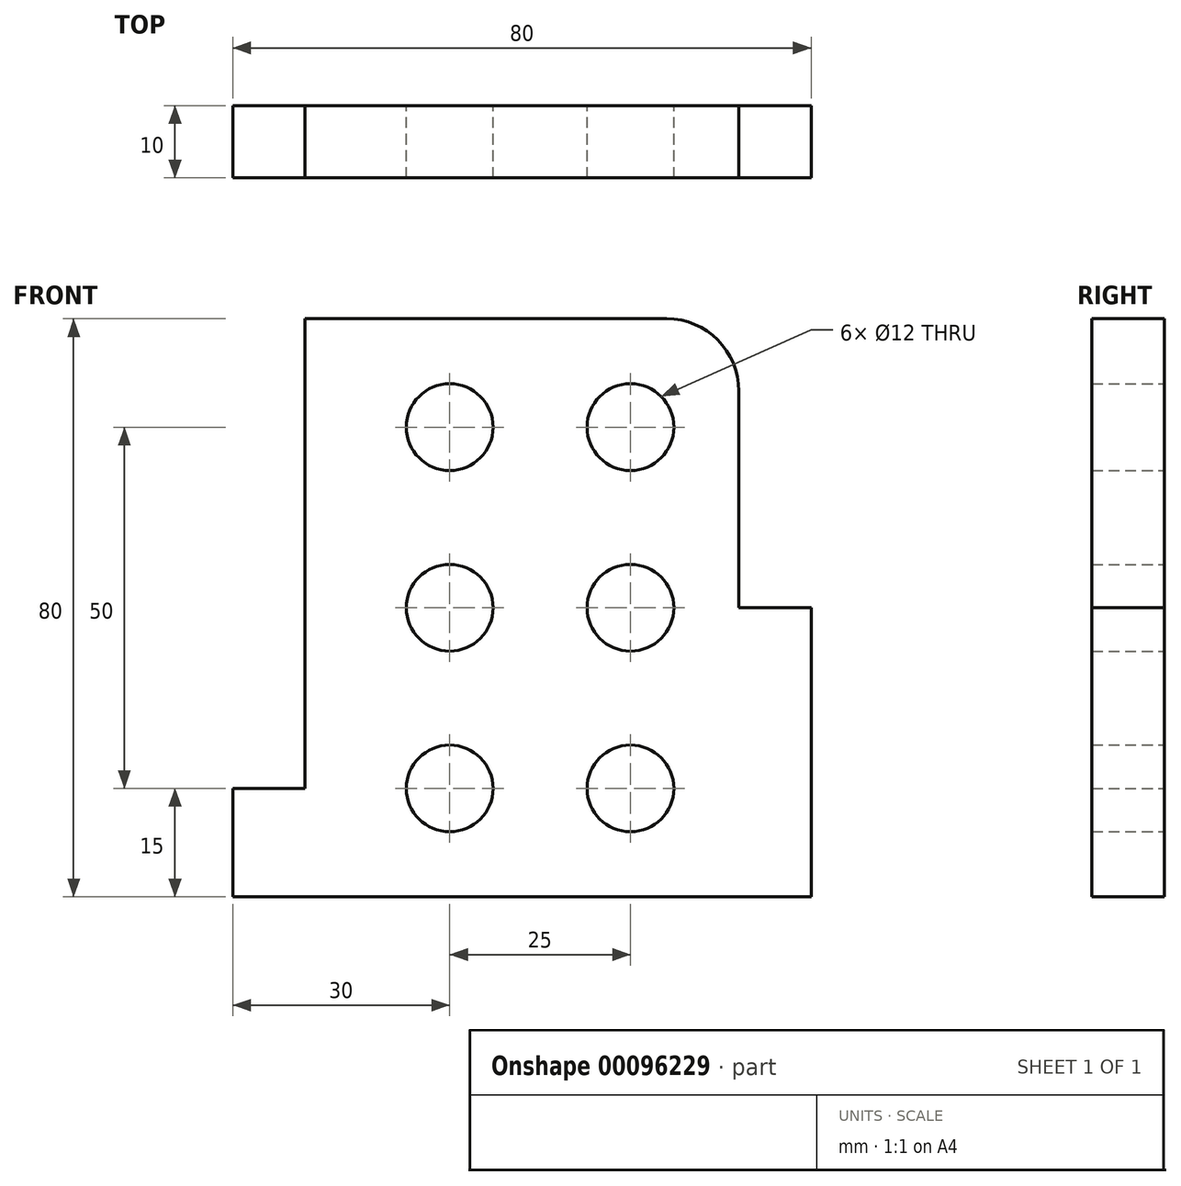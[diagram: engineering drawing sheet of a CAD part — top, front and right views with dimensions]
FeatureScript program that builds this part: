
annotation { "Feature Type Name" : "Feature", "Feature Type Description" : "" }
export const myFeature = defineFeature(function(context is Context, id is Id, definition is map)
    precondition{}
    {
        {
            var Q0;
            Q0=qCreatedBy(makeId("Front.planeOp"),FACE);
            var sketch = newSketch(context, id + "F0", { "sketchPlane" : qUnion([Q0])});
            skLineSegment(sketch, "E0", {"start": v(80, 0) * mm, "end": v(80, 40) * mm});
            skLineSegment(sketch, "E1", {"start": v(80, 40) * mm, "end": v(70, 40) * mm});
            skLineSegment(sketch, "E2", {"start": v(70, 40) * mm, "end": v(70, 70) * mm});
            skLineSegment(sketch, "E3", {"start": v(60, 80) * mm, "end": v(10, 80) * mm});
            skLineSegment(sketch, "E4", {"start": v(10, 80) * mm, "end": v(10, 15) * mm});
            skLineSegment(sketch, "E5", {"start": v(10, 15) * mm, "end": v(0, 15) * mm});
            skLineSegment(sketch, "E6", {"start": v(0, 15) * mm, "end": v(0, 0) * mm});
            skLineSegment(sketch, "E7", {"start": v(0, 0) * mm, "end": v(80, 0) * mm});
            skCircle(sketch, "E8", {"center": v(30, 65) * mm, "radius": 6 * mm});
            skCircle(sketch, "E9", {"center": v(30, 40) * mm, "radius": 6 * mm});
            skCircle(sketch, "E10", {"center": v(30, 15) * mm, "radius": 6 * mm});
            skLineSegment(sketch, "E11", {"start": v(0, 0) * mm, "end": v(30, 0) * mm, "construction": true});
            skLineSegment(sketch, "E12", {"start": v(30, 0) * mm, "end": v(30, 15) * mm, "construction": true});
            skCircle(sketch, "E13", {"center": v(55, 65) * mm, "radius": 6 * mm});
            skCircle(sketch, "E14", {"center": v(55, 40) * mm, "radius": 6 * mm});
            skCircle(sketch, "E15", {"center": v(55, 15) * mm, "radius": 6 * mm});
            skLineSegment(sketch, "E16", {"start": v(0, 0) * mm, "end": v(55, 0) * mm, "construction": true});
            skLineSegment(sketch, "E17", {"start": v(55, 0) * mm, "end": v(55, 15) * mm, "construction": true});
            skLineSegment(sketch, "E18", {"start": v(30, 15) * mm, "end": v(30, 65) * mm, "construction": true});
            skLineSegment(sketch, "E19", {"start": v(55, 40) * mm, "end": v(30, 40) * mm, "construction": true});
            skLineSegment(sketch, "E20", {"start": v(55, 15) * mm, "end": v(30, 15) * mm, "construction": true});
            skLineSegment(sketch, "E21", {"start": v(55, 65) * mm, "end": v(30, 65) * mm, "construction": true});
            skLineSegment(sketch, "E22", {"start": v(55, 65) * mm, "end": v(55, 15) * mm, "construction": true});
            skPoint(sketch, "E23.visualSharp", {"position": v(70, 80) * mm});
            skArc(sketch, "E23.filletArc", {"start": v(70, 70) * mm, "mid": v(67.07, 77.07) * mm, "end": v(60, 80) * mm});
            skSolve(sketch);
        }
        {
            var Q0;
            Q0=makeQuery(id+"F0.imprint","IMPRINT",FACE,{"disambiguationData":[TD([[makeQuery(id+"F0.imprint","IMPRINT",EDGE,{"derivedFrom":sQuery(id+"F0.wireOp",EDGE,"E0")}),1.0]])]});
            extrude(context, id + "F1", {"entities" : qUnion([Q0]), "depth" : 10 * mm});
        }
    });
